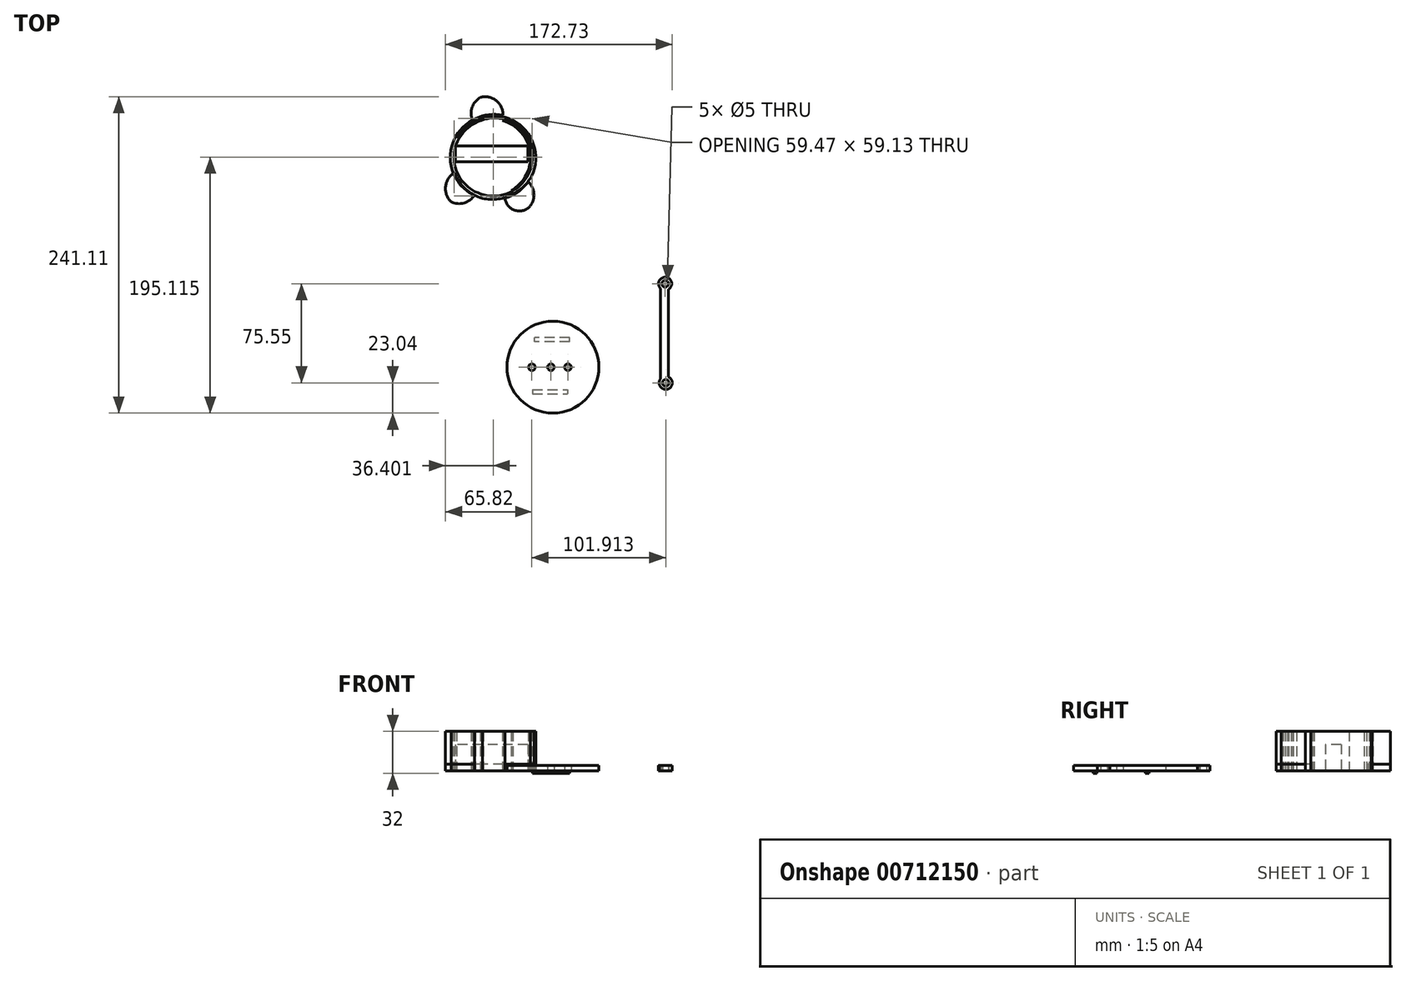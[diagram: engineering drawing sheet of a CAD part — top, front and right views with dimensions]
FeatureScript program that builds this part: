
annotation { "Feature Type Name" : "Feature", "Feature Type Description" : "" }
export const myFeature = defineFeature(function(context is Context, id is Id, definition is map)
    precondition{}
    {
        {
            var Q0;
            Q0=qCreatedBy(makeId("Top.planeOp"),FACE);
            var sketch = newSketch(context, id + "F0", { "sketchPlane" : qUnion([Q0])});
            skCircle(sketch, "E0", {"center": v(0, -2.46) * mm, "radius": 35 * mm});
            skCircle(sketch, "E1", {"center": v(-1.5, -2.46) * mm, "radius": 3 * mm});
            skCircle(sketch, "E2", {"center": v(11.44, -2.46) * mm, "radius": 1.5 * mm});
            skCircle(sketch, "E3", {"center": v(-16, -2.46) * mm, "radius": 1.5 * mm});
            skLineSegment(sketch, "E4.bottom", {"start": v(12.7, 17.02) * mm, "end": v(-13.85, 17.02) * mm});
            skLineSegment(sketch, "E4.top", {"start": v(12.7, 20.02) * mm, "end": v(-13.85, 20.02) * mm});
            skLineSegment(sketch, "E4.left", {"start": v(12.7, 17.02) * mm, "end": v(12.7, 20.02) * mm});
            skLineSegment(sketch, "E4.right", {"start": v(-13.85, 17.02) * mm, "end": v(-13.85, 20.02) * mm});
            skLineSegment(sketch, "E5.bottom", {"start": v(-15.51, -19.66) * mm, "end": v(11.03, -19.66) * mm});
            skLineSegment(sketch, "E5.top", {"start": v(-15.51, -22.66) * mm, "end": v(11.03, -22.66) * mm});
            skLineSegment(sketch, "E5.left", {"start": v(-15.51, -19.66) * mm, "end": v(-15.51, -22.66) * mm});
            skLineSegment(sketch, "E5.right", {"start": v(11.03, -19.66) * mm, "end": v(11.03, -22.66) * mm});
            skSolve(sketch);
        }
        {
            var Q0;
            Q0=makeQuery(id+"F0.imprint","IMPRINT",FACE,{"disambiguationData":[TD([[makeQuery(id+"F0.imprint","IMPRINT",EDGE,{"derivedFrom":sQuery(id+"F0.wireOp",EDGE,"E4.bottom")}),-1.0]])]});
            var Q1;
            Q1=makeQuery(id+"F0.imprint","IMPRINT",FACE,{"disambiguationData":[TD([[makeQuery(id+"F0.imprint","IMPRINT",EDGE,{"derivedFrom":sQuery(id+"F0.wireOp",EDGE,"E5.bottom")}),-1.0]])]});
            var Q2;
            Q2=makeQuery(id+"F0.imprint","IMPRINT",FACE,{"disambiguationData":[TD([[makeQuery(id+"F0.imprint","IMPRINT",EDGE,{"derivedFrom":sQuery(id+"F0.wireOp",EDGE,"E0")}),1.0]])]});
            var Q3;
            Q3=makeQuery(id+"F0.imprint","IMPRINT",FACE,{"disambiguationData":[TD([[makeQuery(id+"F0.imprint","IMPRINT",EDGE,{"derivedFrom":sQuery(id+"F0.wireOp",EDGE,"E2")}),1.0]])]});
            var Q4;
            Q4=makeQuery(id+"F0.imprint","IMPRINT",FACE,{"disambiguationData":[TD([[makeQuery(id+"F0.imprint","IMPRINT",EDGE,{"derivedFrom":sQuery(id+"F0.wireOp",EDGE,"E1")}),1.0]])]});
            var Q5;
            Q5=makeQuery(id+"F0.imprint","IMPRINT",FACE,{"disambiguationData":[TD([[makeQuery(id+"F0.imprint","IMPRINT",EDGE,{"derivedFrom":sQuery(id+"F0.wireOp",EDGE,"E3")}),1.0]])]});
            extrude(context, id + "F1", {"entities" : qUnion([Q0, Q1, Q2, Q3, Q4, Q5]), "depth" : 4 * mm, "offsetDistance" : 25 * mm});
        }
        {
            var Q0;
            Q0=makeQuery(id+"F0.imprint","IMPRINT",FACE,{"disambiguationData":[TD([[makeQuery(id+"F0.imprint","IMPRINT",EDGE,{"derivedFrom":sQuery(id+"F0.wireOp",EDGE,"E5.bottom")}),-1.0]])]});
            var Q1;
            Q1=makeQuery(id+"F0.imprint","IMPRINT",FACE,{"disambiguationData":[TD([[makeQuery(id+"F0.imprint","IMPRINT",EDGE,{"derivedFrom":sQuery(id+"F0.wireOp",EDGE,"E4.bottom")}),-1.0]])]});
            extrude(context, id + "F2", {"entities" : qUnion([Q0, Q1]), "operationType" : NewBodyOperationType.ADD, "oppositeDirection" : true, "depth" : 2 * mm, "offsetDistance" : 25 * mm});
        }
        {
            var Q0;
            Q0=sQuery(id+"F0.wireOp",VERTEX,"E1.center");
            var Q1;
            Q1=sQuery(id+"F0.wireOp",VERTEX,"E2.center");
            var Q2;
            Q2=sQuery(id+"F0.wireOp",VERTEX,"E3.center");
            var Q3;
            Q3=makeQuery(id+"F1.opExtrude","SWEPT_BODY",BODY,{"disambiguationData":[OSD([sQuery(id+"F0.wireOp",EDGE,"E0")])]});
            hole(context, id + "F3", {"style" : HoleStyle.SIMPLE, "endStyle" : HoleEndStyle.THROUGH, "oppositeDirection" : true, "holeDiameter" : 5 * mm, "majorDiameter" : 5 * mm, "isTappedThrough" : true, "tappedDepth" : 12 * mm, "tapClearance" : 3, "locations" : qUnion([Q0, Q1, Q2]), "scope" : qUnion([Q3])});
        }
        {
            var Q0;
            Q0=qCreatedBy(makeId("Top.planeOp"),FACE);
            var sketch = newSketch(context, id + "F4", { "sketchPlane" : qUnion([Q0])});
            skCircle(sketch, "E6", {"center": v(85.45, 61.13) * mm, "radius": 5 * mm});
            skLineSegment(sketch, "E7.bottom", {"start": v(81.95, 57.57) * mm, "end": v(87.95, 57.57) * mm});
            skLineSegment(sketch, "E7.top", {"start": v(81.95, -12.43) * mm, "end": v(87.95, -12.43) * mm});
            skLineSegment(sketch, "E7.left", {"start": v(81.95, 57.57) * mm, "end": v(81.95, -12.43) * mm});
            skLineSegment(sketch, "E7.right", {"start": v(87.95, 57.57) * mm, "end": v(87.95, -12.43) * mm});
            skLineSegment(sketch, "E8.bottom", {"start": v(106.8, 41.7) * mm, "end": v(106.92, 41.7) * mm});
            skLineSegment(sketch, "E8.top", {"start": v(106.8, 42.46) * mm, "end": v(106.92, 42.46) * mm});
            skLineSegment(sketch, "E8.left", {"start": v(106.8, 41.7) * mm, "end": v(106.8, 42.46) * mm});
            skLineSegment(sketch, "E8.right", {"start": v(106.92, 41.7) * mm, "end": v(106.92, 42.46) * mm});
            skCircle(sketch, "E9", {"center": v(85.91, -14.42) * mm, "radius": 5 * mm});
            skSolve(sketch);
        }
        {
            var Q0;
            {var subQ0=sQuery(id+"F4.wireOp",EDGE,"E7.bottom");Q0=makeQuery(id+"F4.imprint","IMPRINT",FACE,{"disambiguationData":[TD([[makeQuery(id+"F4.imprint","IMPRINT",EDGE,{"derivedFrom":subQ0}),1.0]])]});}
            var Q1;
            {var subQ0=sQuery(id+"F4.wireOp",EDGE,"E7.top");Q1=makeQuery(id+"F4.imprint","IMPRINT",FACE,{"disambiguationData":[TD([[makeQuery(id+"F4.imprint","IMPRINT",EDGE,{"derivedFrom":subQ0}),-1.0]])]});}
            var Q2;
            {var subQ1=sQuery(id+"F4.wireOp",EDGE,"E6");var subQ3=sQuery(id+"F4.wireOp",EDGE,"E7.right");var subQ4=makeQuery(id+"F4.imprint","INTERSECT",VERTEX,{"derivedFrom":[subQ1,subQ3]});Q2=makeQuery(id+"F4.imprint","IMPRINT",FACE,{"disambiguationData":[TD([[makeQuery(id+"F4.imprint","IMPRINT",EDGE,{"disambiguationData":[TD([[subQ4,-1.0]])],"derivedFrom":subQ3}),-1.0]])]});}
            var Q3;
            {var subQ0=sQuery(id+"F4.wireOp",EDGE,"E7.bottom");Q3=makeQuery(id+"F4.imprint","IMPRINT",FACE,{"disambiguationData":[TD([[makeQuery(id+"F4.imprint","IMPRINT",EDGE,{"derivedFrom":subQ0}),-1.0]])]});}
            var Q4;
            {var subQ0=sQuery(id+"F4.wireOp",EDGE,"E7.top");Q4=makeQuery(id+"F4.imprint","IMPRINT",FACE,{"disambiguationData":[TD([[makeQuery(id+"F4.imprint","IMPRINT",EDGE,{"derivedFrom":subQ0}),1.0]])]});}
            extrude(context, id + "F5", {"entities" : qUnion([Q0, Q1, Q2, Q3, Q4]), "depth" : 4 * mm, "offsetDistance" : 25 * mm});
        }
        {
            var Q0;
            Q0=sQuery(id+"F4.wireOp",VERTEX,"E6.center");
            var Q1;
            Q1=sQuery(id+"F4.wireOp",VERTEX,"E9.center");
            var Q2;
            Q2=makeQuery(id+"F5.opExtrude","SWEPT_BODY",BODY,{"disambiguationData":[OSD([sQuery(id+"F4.wireOp",EDGE,"E6"),sQuery(id+"F4.wireOp",EDGE,"E7.left"),sQuery(id+"F4.wireOp",EDGE,"E7.right"),sQuery(id+"F4.wireOp",EDGE,"E9")])]});
            hole(context, id + "F6", {"style" : HoleStyle.SIMPLE, "endStyle" : HoleEndStyle.THROUGH, "oppositeDirection" : true, "holeDiameter" : 5 * mm, "majorDiameter" : 5 * mm, "isTappedThrough" : true, "tappedDepth" : 12 * mm, "tapClearance" : 3, "locations" : qUnion([Q0, Q1]), "scope" : qUnion([Q2])});
        }
        {
            var Q0;
            Q0=qCreatedBy(makeId("Top.planeOp"),FACE);
            var sketch = newSketch(context, id + "F7", { "sketchPlane" : qUnion([Q0])});
            skLineSegment(sketch, "E10.bottom", {"start": v(82.24, 55.57) * mm, "end": v(84.24, 55.57) * mm});
            skLineSegment(sketch, "E10.top", {"start": v(82.24, -9.43) * mm, "end": v(84.24, -9.43) * mm});
            skLineSegment(sketch, "E10.left", {"start": v(82.24, 55.57) * mm, "end": v(82.24, -9.43) * mm});
            skLineSegment(sketch, "E10.right", {"start": v(84.24, 55.57) * mm, "end": v(84.24, -9.43) * mm});
            skSolve(sketch);
        }
        {
            var Q0;
            Q0 = qSketchRegion(id + "F7", true);
            extrude(context, id + "F8", {"entities" : qUnion([Q0]), "operationType" : NewBodyOperationType.ADD, "depth" : 3 * mm, "offsetDistance" : 25 * mm});
        }
        {
            var Q0;
            Q0=qCreatedBy(makeId("Top.planeOp"),FACE);
            var sketch = newSketch(context, id + "F9", { "sketchPlane" : qUnion([Q0])});
            skCircle(sketch, "E11", {"center": v(-45.09, 157.13) * mm, "radius": 32 * mm});
            skCircle(sketch, "E12", {"center": v(-45.09, 157.13) * mm, "radius": 29.13 * mm});
            skArc(sketch, "E13", {"start": v(-77.49, 123.57) * mm, "mid": v(-67.6, 122.68) * mm, "end": v(-59.7, 128.66) * mm});
            skArc(sketch, "E14", {"start": v(-75, 145.76) * mm, "mid": v(-81.73, 135.28) * mm, "end": v(-77.49, 123.57) * mm});
            skCircle(sketch, "E15", {"center": v(-44.48, 158.33) * mm, "radius": 32 * mm});
            skCircle(sketch, "E16", {"center": v(-44.48, 158.33) * mm, "radius": 29.13 * mm});
            skArc(sketch, "E17", {"start": v(-17.06, 120.6) * mm, "mid": v(-14.46, 130.17) * mm, "end": v(-18.98, 139) * mm});
            skArc(sketch, "E18", {"start": v(-38.32, 190.37) * mm, "mid": v(-50.84, 187.94) * mm, "end": v(-55.87, 176.21) * mm});
            skCircle(sketch, "E19", {"center": v(-46.2, 157.42) * mm, "radius": 32 * mm});
            skCircle(sketch, "E20", {"center": v(-46.2, 157.42) * mm, "radius": 29.13 * mm});
            skArc(sketch, "E21", {"start": v(-55.1, 203.2) * mm, "mid": v(-61.5, 195.63) * mm, "end": v(-61.15, 185.71) * mm});
            skArc(sketch, "E22", {"start": v(-38.11, 188.38) * mm, "mid": v(-42.69, 200.29) * mm, "end": v(-55.1, 203.2) * mm});
            skArc(sketch, "E23", {"start": v(-36.54, 126.3) * mm, "mid": v(-28.68, 117.02) * mm, "end": v(-17.06, 120.6) * mm});
            skSolve(sketch);
        }
        {
            var Q0;
            Q0=makeQuery(id+"F9.imprint","IMPRINT",FACE,{"disambiguationData":[TD([[makeQuery(id+"F9.imprint","IMPRINT",EDGE,{"derivedFrom":sQuery(id+"F9.wireOp",EDGE,"E11")}),1.0]])]});
            var Q1;
            {var subQ1=sQuery(id+"F9.wireOp",EDGE,"E11");var subQ5=sQuery(id+"F9.wireOp",EDGE,"E14");var subQ6=makeQuery(id+"F9.imprint","INTERSECT",VERTEX,{"derivedFrom":[subQ1,subQ5]});Q1=makeQuery(id+"F9.imprint","IMPRINT",FACE,{"disambiguationData":[TD([[makeQuery(id+"F9.imprint","IMPRINT",EDGE,{"disambiguationData":[TD([[subQ6,1.0]])],"derivedFrom":subQ1}),-1.0]])]});}
            var Q2;
            {var subQ0=sQuery(id+"F9.wireOp",EDGE,"E21");Q2=makeQuery(id+"F9.imprint","IMPRINT",FACE,{"disambiguationData":[TD([[makeQuery(id+"F9.imprint","IMPRINT",EDGE,{"derivedFrom":subQ0}),1.0]])]});}
            var Q3;
            {var subQ0=sQuery(id+"F9.wireOp",EDGE,"E14");var subQ1=sQuery(id+"F9.wireOp",EDGE,"E13");var subQ2=makeQuery(id+"F9.imprint","INTERSECT",VERTEX,{"derivedFrom":[subQ1,subQ0]});Q3=makeQuery(id+"F9.imprint","IMPRINT",FACE,{"disambiguationData":[TD([[makeQuery(id+"F9.imprint","IMPRINT",EDGE,{"disambiguationData":[TD([[subQ2,-1.0]])],"derivedFrom":subQ1}),1.0]])]});}
            var Q4;
            {var subQ0=sQuery(id+"F9.wireOp",EDGE,"E15");var subQ1=sQuery(id+"F9.wireOp",EDGE,"E11");var subQ2=makeQuery(id+"F9.imprint","INTERSECT",VERTEX,{"disambiguationData":[OD(0.0)],"derivedFrom":[subQ1,subQ0]});Q4=makeQuery(id+"F9.imprint","IMPRINT",FACE,{"disambiguationData":[TD([[makeQuery(id+"F9.imprint","IMPRINT",EDGE,{"disambiguationData":[TD([[subQ2,-1.0]])],"derivedFrom":subQ1}),1.0]])]});}
            var Q5;
            {var subQ0=sQuery(id+"F9.wireOp",EDGE,"E23");Q5=makeQuery(id+"F9.imprint","IMPRINT",FACE,{"disambiguationData":[TD([[makeQuery(id+"F9.imprint","IMPRINT",EDGE,{"derivedFrom":subQ0}),1.0]])]});}
            var Q6;
            {var subQ5=sQuery(id+"F9.wireOp",EDGE,"E18");var subQ6=sQuery(id+"F9.wireOp",EDGE,"E11");var subQ7=makeQuery(id+"F9.imprint","INTERSECT",VERTEX,{"derivedFrom":[subQ6,subQ5]});Q6=makeQuery(id+"F9.imprint","IMPRINT",FACE,{"disambiguationData":[TD([[makeQuery(id+"F9.imprint","IMPRINT",EDGE,{"disambiguationData":[TD([[subQ7,1.0]])],"derivedFrom":subQ6}),1.0]])]});}
            var Q7;
            {var subQ0=sQuery(id+"F9.wireOp",EDGE,"E20");var subQ1=sQuery(id+"F9.wireOp",EDGE,"E12");var subQ2=makeQuery(id+"F9.imprint","INTERSECT",VERTEX,{"disambiguationData":[OD(0.0)],"derivedFrom":[subQ1,subQ0]});Q7=makeQuery(id+"F9.imprint","IMPRINT",FACE,{"disambiguationData":[TD([[makeQuery(id+"F9.imprint","IMPRINT",EDGE,{"disambiguationData":[TD([[subQ2,1.0]])],"derivedFrom":subQ1}),1.0]])]});}
            extrude(context, id + "F10", {"entities" : qUnion([Q0, Q1, Q2, Q3, Q4, Q5, Q6, Q7]), "depth" : 30 * mm, "offsetDistance" : 25 * mm});
        }
        {
            var Q0;
            {var subQ0=sQuery(id+"F9.wireOp",EDGE,"E14");var subQ1=sQuery(id+"F9.wireOp",EDGE,"E13");var subQ2=makeQuery(id+"F9.imprint","INTERSECT",VERTEX,{"derivedFrom":[subQ1,subQ0]});Q0=makeQuery(id+"F9.imprint","IMPRINT",FACE,{"disambiguationData":[TD([[makeQuery(id+"F9.imprint","IMPRINT",EDGE,{"disambiguationData":[TD([[subQ2,-1.0]])],"derivedFrom":subQ1}),1.0]])]});}
            var Q1;
            {var subQ0=sQuery(id+"F9.wireOp",EDGE,"E23");Q1=makeQuery(id+"F9.imprint","IMPRINT",FACE,{"disambiguationData":[TD([[makeQuery(id+"F9.imprint","IMPRINT",EDGE,{"derivedFrom":subQ0}),1.0]])]});}
            var Q2;
            {var subQ0=sQuery(id+"F9.wireOp",EDGE,"E21");Q2=makeQuery(id+"F9.imprint","IMPRINT",FACE,{"disambiguationData":[TD([[makeQuery(id+"F9.imprint","IMPRINT",EDGE,{"derivedFrom":subQ0}),1.0]])]});}
            extrude(context, id + "F11", {"entities" : qUnion([Q0, Q1, Q2]), "depth" : 5 * mm, "offsetDistance" : 25 * mm});
        }
        {
            var Q0;
            Q0=qCreatedBy(makeId("Top.planeOp"),FACE);
            var sketch = newSketch(context, id + "F12", { "sketchPlane" : qUnion([Q0])});
            skLineSegment(sketch, "E24.bottom", {"start": v(-19.12, 166.13) * mm, "end": v(-74.12, 166.13) * mm});
            skLineSegment(sketch, "E24.top", {"start": v(-19.12, 154.13) * mm, "end": v(-74.12, 154.13) * mm});
            skLineSegment(sketch, "E24.left", {"start": v(-19.12, 166.13) * mm, "end": v(-19.12, 154.13) * mm});
            skLineSegment(sketch, "E24.right", {"start": v(-74.12, 166.13) * mm, "end": v(-74.12, 154.13) * mm});
            skLineSegment(sketch, "E25.bottom", {"start": v(-61.8, 154.13) * mm, "end": v(-74.12, 154.13) * mm});
            skLineSegment(sketch, "E25.top", {"start": v(-61.8, 166.13) * mm, "end": v(-74.12, 166.13) * mm});
            skLineSegment(sketch, "E25.left", {"start": v(-61.8, 154.13) * mm, "end": v(-61.8, 166.13) * mm});
            skLineSegment(sketch, "E25.right", {"start": v(-74.12, 154.13) * mm, "end": v(-74.12, 166.13) * mm});
            skSolve(sketch);
        }
        {
            var Q0;
            Q0 = qSketchRegion(id + "F12", true);
            extrude(context, id + "F13", {"entities" : qUnion([Q0]), "depth" : 20 * mm, "offsetDistance" : 25 * mm});
        }
    });
